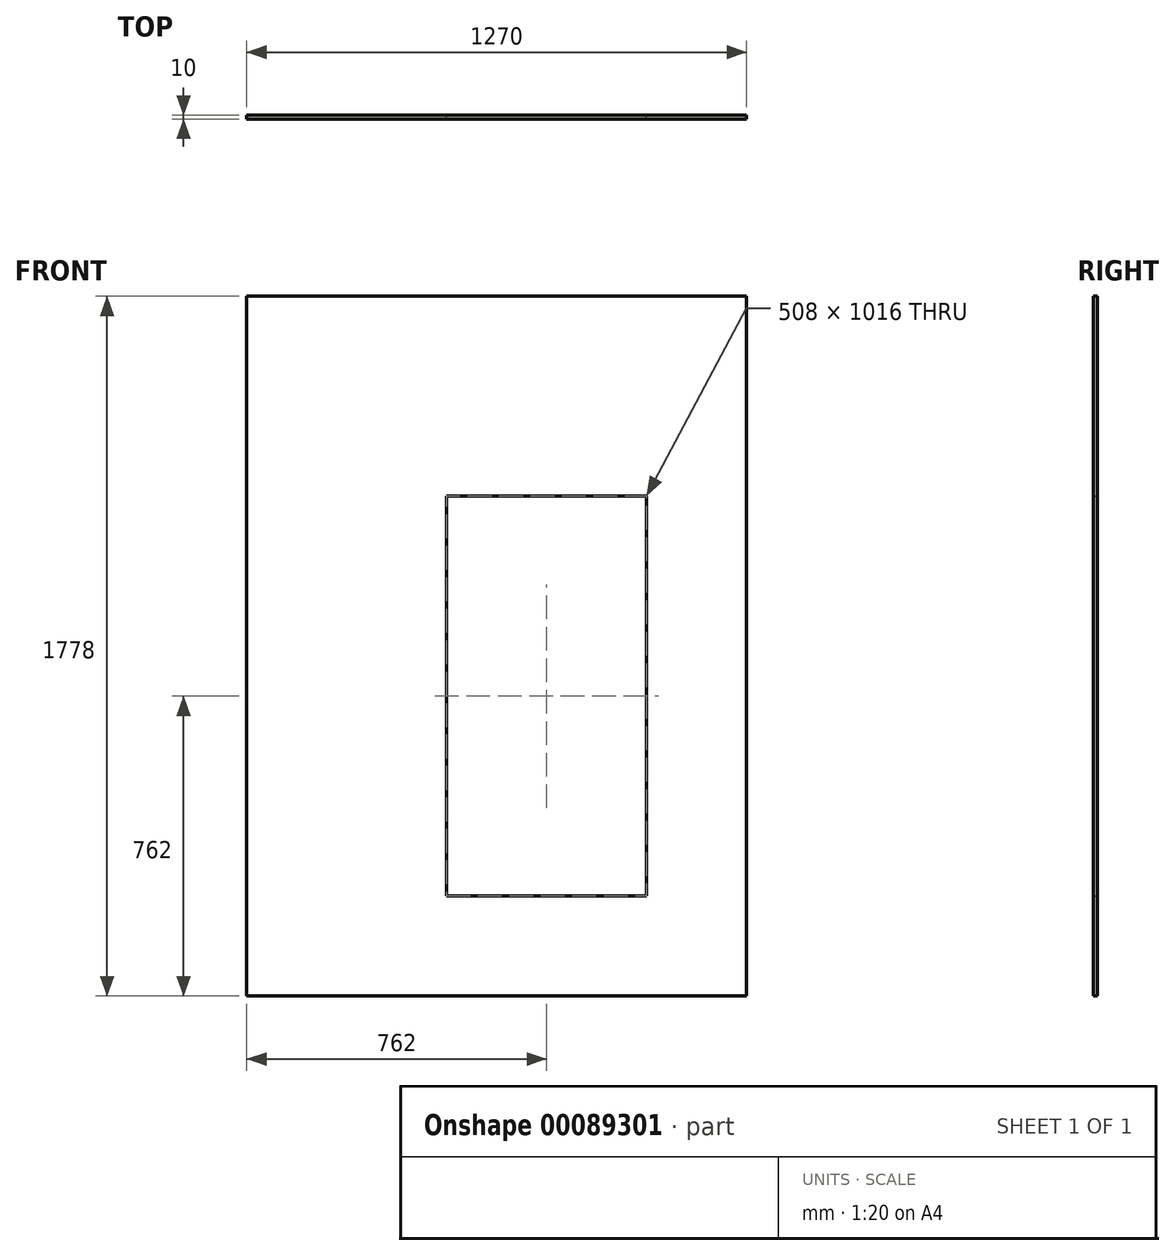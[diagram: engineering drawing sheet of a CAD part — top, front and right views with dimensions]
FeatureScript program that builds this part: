
annotation { "Feature Type Name" : "Feature", "Feature Type Description" : "" }
export const myFeature = defineFeature(function(context is Context, id is Id, definition is map)
    precondition{}
    {
        {
            var Q0;
            Q0=qCreatedBy(makeId("Front.planeOp"),FACE);
            var sketch = newSketch(context, id + "F0", { "sketchPlane" : qUnion([Q0])});
            skLineSegment(sketch, "E0", {"start": v(0, 0) * mm, "end": v(0, 1778) * mm});
            skLineSegment(sketch, "E1", {"start": v(0, 0) * mm, "end": v(1270, 0) * mm});
            skLineSegment(sketch, "E2", {"start": v(1270, 0) * mm, "end": v(1270, 1778) * mm});
            skLineSegment(sketch, "E3", {"start": v(0, 1778) * mm, "end": v(1270, 1778) * mm});
            skLineSegment(sketch, "E4.bottom", {"start": v(508, 1270) * mm, "end": v(1016, 1270) * mm});
            skLineSegment(sketch, "E4.top", {"start": v(508, 254) * mm, "end": v(1016, 254) * mm});
            skLineSegment(sketch, "E4.left", {"start": v(508, 1270) * mm, "end": v(508, 254) * mm});
            skLineSegment(sketch, "E4.right", {"start": v(1016, 1270) * mm, "end": v(1016, 254) * mm});
            skSolve(sketch);
        }
        {
            var Q0;
            Q0 = qSketchRegion(id + "F0", true);
            extrude(context, id + "F1", {"entities" : qUnion([Q0]), "depth" : 10 * mm});
        }
    });
